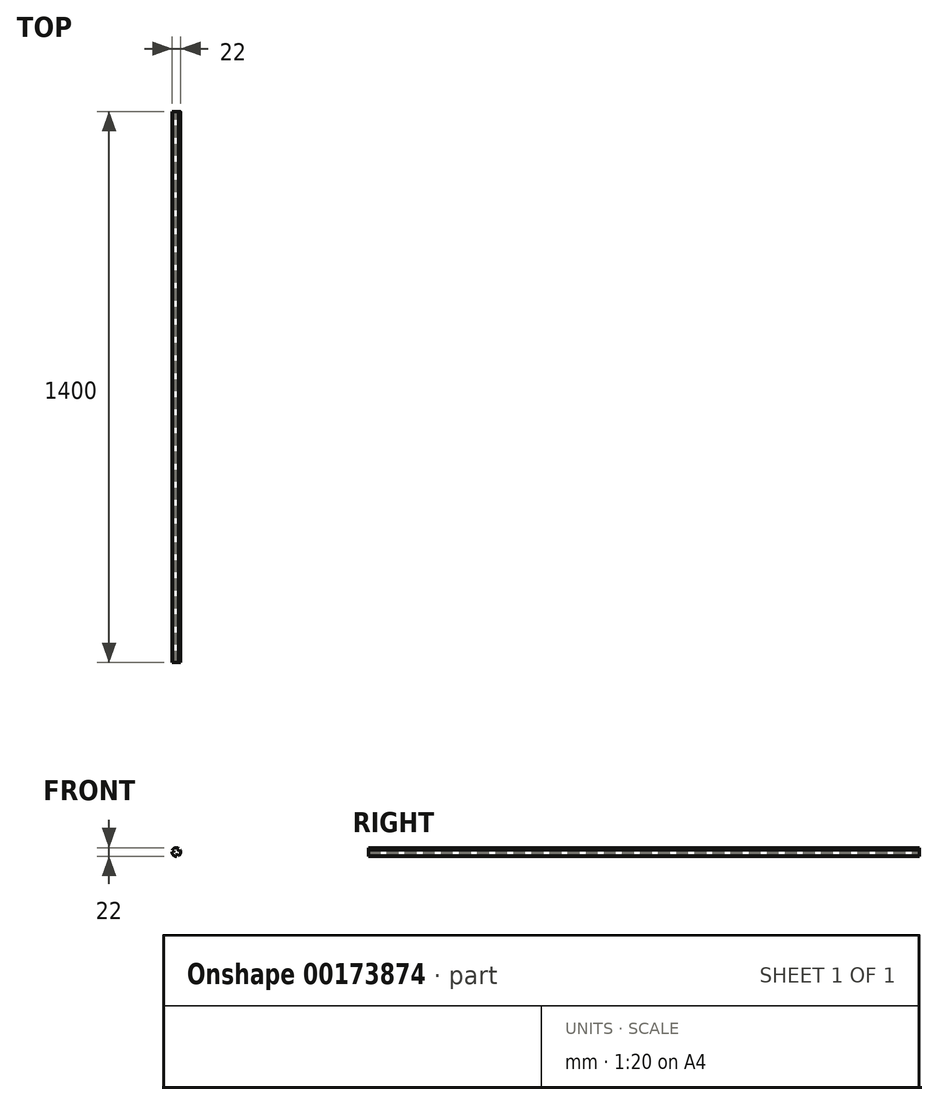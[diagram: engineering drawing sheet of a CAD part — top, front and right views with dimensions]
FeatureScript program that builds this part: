
annotation { "Feature Type Name" : "Feature", "Feature Type Description" : "" }
export const myFeature = defineFeature(function(context is Context, id is Id, definition is map)
    precondition{}
    {
        {
            var Q0;
            Q0=qCreatedBy(makeId("Front.planeOp"),FACE);
            var sketch = newSketch(context, id + "F0", { "sketchPlane" : qUnion([Q0])});
            skArc(sketch, "E0", {"start": v(5.8, 9.34) * mm, "mid": v(-2.85, 10.63) * mm, "end": v(-9.7, 5.19) * mm});
            skLineSegment(sketch, "E1", {"start": v(0, 0) * mm, "end": v(0, 11) * mm, "construction": true});
            skLineSegment(sketch, "E2", {"start": v(0, 0) * mm, "end": v(7.78, 7.78) * mm, "construction": true});
            skLineSegment(sketch, "E3.0", {"start": v(6.51, 2.98) * mm, "end": v(9.34, 5.8) * mm});
            skLineSegment(sketch, "E4", {"start": v(2.98, 6.51) * mm, "end": v(6.51, 2.98) * mm});
            skLineSegment(sketch, "E5.trimOffspring", {"start": v(2.98, 6.51) * mm, "end": v(5.8, 9.34) * mm});
            skLineSegment(sketch, "E6.1.0", {"start": v(-7.13, -0.68) * mm, "end": v(-11, 0.36) * mm});
            skLineSegment(sketch, "E6.1.1", {"start": v(-7.13, -0.68) * mm, "end": v(-5.84, 4.15) * mm});
            skLineSegment(sketch, "E6.1.2", {"start": v(-5.84, 4.15) * mm, "end": v(-9.7, 5.19) * mm});
            skLineSegment(sketch, "E6.2.0", {"start": v(4.15, -5.84) * mm, "end": v(5.19, -9.7) * mm});
            skLineSegment(sketch, "E6.2.1", {"start": v(4.15, -5.84) * mm, "end": v(-0.68, -7.13) * mm});
            skLineSegment(sketch, "E6.2.2", {"start": v(-0.68, -7.13) * mm, "end": v(0.36, -11) * mm});
            skArc(sketch, "E7.trimOffspring", {"start": v(5.19, -9.7) * mm, "mid": v(10.63, -2.85) * mm, "end": v(9.34, 5.8) * mm});
            skArc(sketch, "E8.trimOffspring", {"start": v(-11, 0.36) * mm, "mid": v(-7.78, -7.78) * mm, "end": v(0.36, -11) * mm});
            skSolve(sketch);
        }
        {
            var Q0;
            Q0 = qSketchRegion(id + "F0", true);
            extrude(context, id + "F1", {"entities" : qUnion([Q0]), "depth" : 1400 * mm});
        }
    });
